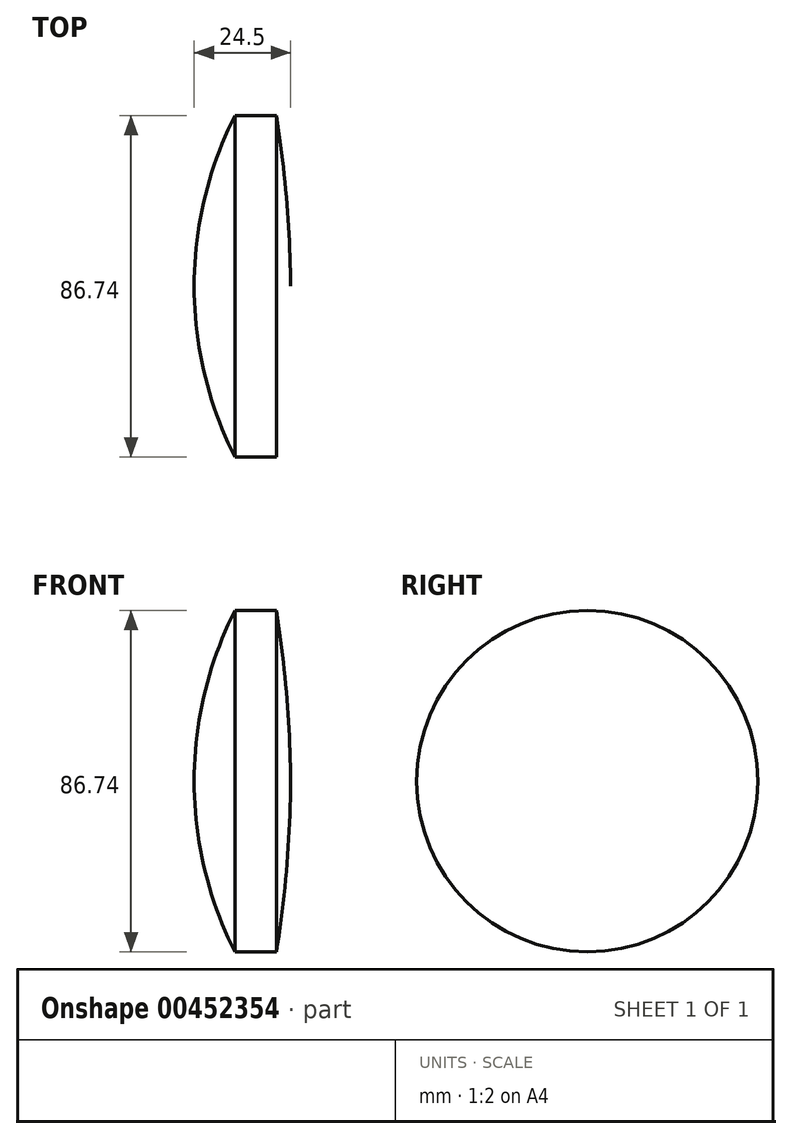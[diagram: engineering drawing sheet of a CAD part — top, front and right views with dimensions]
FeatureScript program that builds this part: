
annotation { "Feature Type Name" : "Feature", "Feature Type Description" : "" }
export const myFeature = defineFeature(function(context is Context, id is Id, definition is map)
    precondition{}
    {
        {
            var Q0;
            Q0=qCreatedBy(makeId("Front.planeOp"),FACE);
            var sketch = newSketch(context, id + "F0", { "sketchPlane" : qUnion([Q0])});
            skArc(sketch, "E0", {"start": v(0, 43.37) * mm, "mid": v(-7.7, 22.29) * mm, "end": v(-10.34, 0) * mm});
            skLineSegment(sketch, "E1", {"start": v(0, 43.37) * mm, "end": v(10.52, 43.37) * mm});
            skArc(sketch, "E2", {"start": v(14.15, 0) * mm, "mid": v(13.17, 21.75) * mm, "end": v(10.52, 43.37) * mm});
            skPoint(sketch, "E3.start.orphan", {"position": v(0, -43.73) * mm});
            skLineSegment(sketch, "E4", {"start": v(-10.34, 0) * mm, "end": v(14.15, 0) * mm});
            skSolve(sketch);
        }
        {
            var Q0;
            Q0=qCreatedBy(makeId("Front.planeOp"),FACE);
            var sketch = newSketch(context, id + "F1", { "sketchPlane" : qUnion([Q0])});
            skLineSegment(sketch, "E5", {"start": v(-39.01, 0) * mm, "end": v(45.9, 0) * mm, "construction": true});
            skSolve(sketch);
        }
        {
            var Q0;
            Q0 = qSketchRegion(id + "F0", true);
            var Q1;
            Q1=sQuery(id+"F1.wireOp",EDGE,"E5");
            revolve(context, id + "F2", {"entities" : qUnion([Q0]), "axis" : qUnion([Q1]), "revolveType" : RevolveType.FULL});
        }
    });
